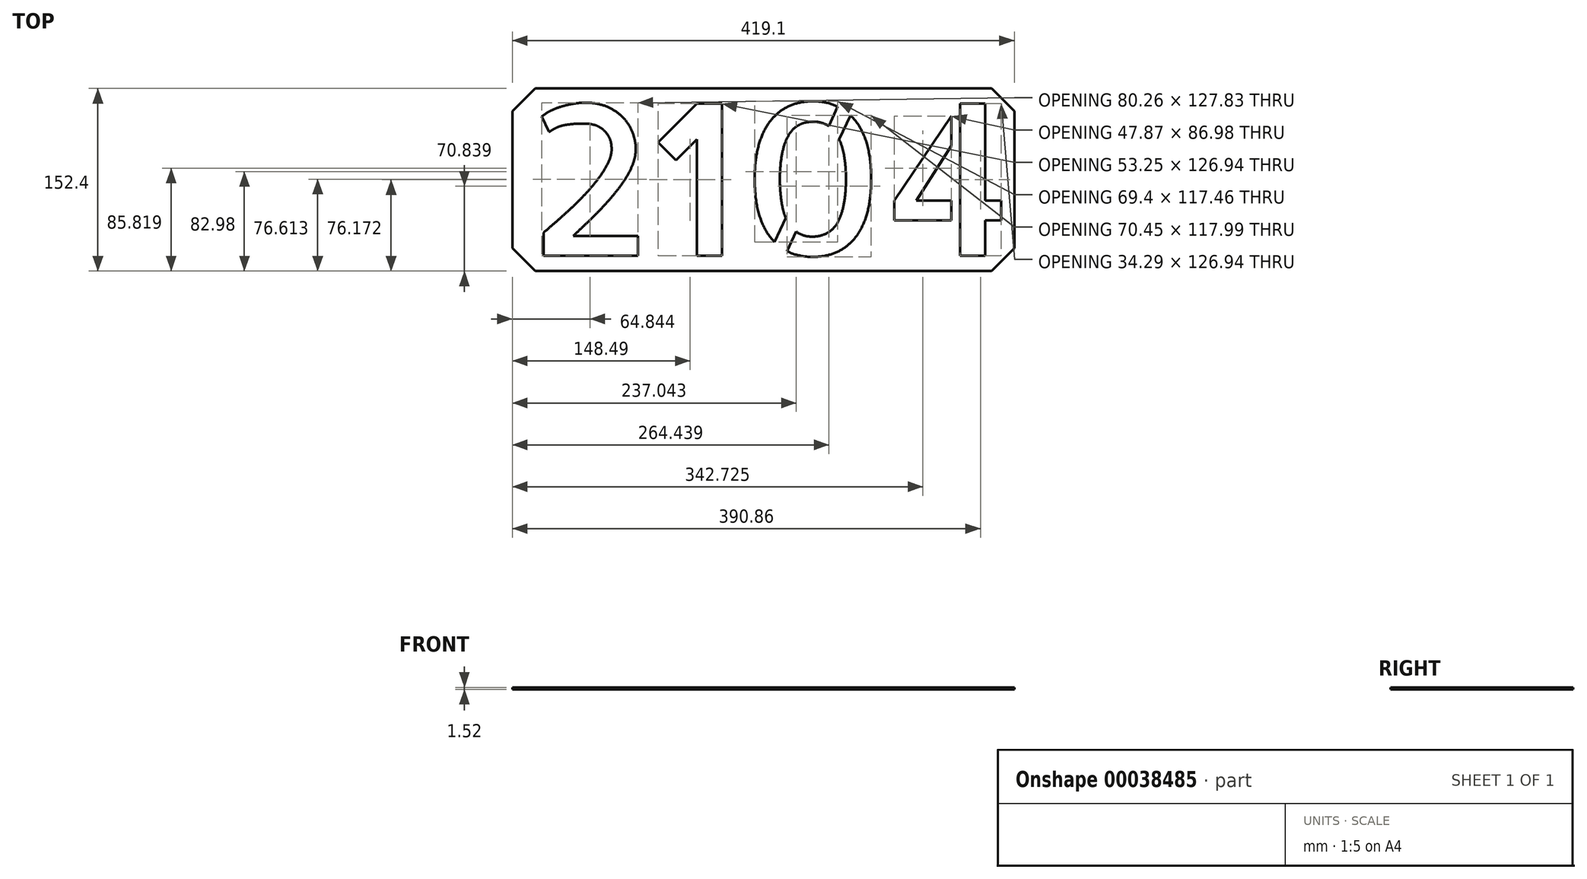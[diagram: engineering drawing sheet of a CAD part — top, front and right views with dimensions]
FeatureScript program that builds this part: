
annotation { "Feature Type Name" : "Feature", "Feature Type Description" : "" }
export const myFeature = defineFeature(function(context is Context, id is Id, definition is map)
    precondition{}
    {
        {
            var Q0;
            Q0=qCreatedBy(makeId("Top.planeOp"),FACE);
            var sketch = newSketch(context, id + "F0", { "sketchPlane" : qUnion([Q0])});
            skText(sketch, "E0", { "text": "2104", "fontName": "AllertaStencil-Regular.ttf"});
            const initialGuessF0  = {"E0": [-0.19845, -0.0635, 1, 0, 0.127]};
            skSetInitialGuess(sketch, initialGuessF0);
            skSolve(sketch);
        }
        {
            var Q0;
            Q0=qCreatedBy(makeId("Top.planeOp"),FACE);
            var sketch = newSketch(context, id + "F1", { "sketchPlane" : qUnion([Q0])});
            skLineSegment(sketch, "E1.rect.bottom", {"start": v(209.55, -76.2) * mm, "end": v(-209.55, -76.2) * mm});
            skLineSegment(sketch, "E1.rect.top", {"start": v(209.55, 76.2) * mm, "end": v(-209.55, 76.2) * mm});
            skLineSegment(sketch, "E1.rect.left", {"start": v(209.55, -76.2) * mm, "end": v(209.55, 76.2) * mm});
            skLineSegment(sketch, "E1.rect.right", {"start": v(-209.55, -76.2) * mm, "end": v(-209.55, 76.2) * mm});
            skPoint(sketch, "E1.rect.middle", {"position": v(0, 0) * mm});
            skSolve(sketch);
        }
        {
            var Q0;
            Q0 = qSketchRegion(id + "F1", true);
            extrude(context, id + "F2", {"entities" : qUnion([Q0]), "depth" : 1.52 * mm});
        }
        {
            var Q0;
            Q0 = qSketchRegion(id + "F0", true);
            extrude(context, id + "F3", {"entities" : qUnion([Q0]), "operationType" : NewBodyOperationType.REMOVE, "depth" : 25.4 * mm});
        }
        {
            var Q0;
            Q0=makeQuery(id+"F2.opExtrude","SWEPT_EDGE",EDGE,{"disambiguationData":[OSD([sQuery(id+"F1.wireOp",EDGE,"E1.rect.bottom"),sQuery(id+"F1.wireOp",EDGE,"E1.rect.left")])]});
            var Q1;
            Q1=makeQuery(id+"F2.opExtrude","SWEPT_EDGE",EDGE,{"disambiguationData":[OSD([sQuery(id+"F1.wireOp",EDGE,"E1.rect.top"),sQuery(id+"F1.wireOp",EDGE,"E1.rect.left")])]});
            var Q2;
            Q2=makeQuery(id+"F2.opExtrude","SWEPT_EDGE",EDGE,{"disambiguationData":[OSD([sQuery(id+"F1.wireOp",EDGE,"E1.rect.bottom"),sQuery(id+"F1.wireOp",EDGE,"E1.rect.right")])]});
            var Q3;
            Q3=makeQuery(id+"F2.opExtrude","SWEPT_EDGE",EDGE,{"disambiguationData":[OSD([sQuery(id+"F1.wireOp",EDGE,"E1.rect.top"),sQuery(id+"F1.wireOp",EDGE,"E1.rect.right")])]});
            chamfer(context, id + "F4", {"entities" : qUnion([Q0, Q1, Q2, Q3]), "width" : 19.05 * mm, "tangentPropagation" : true});
        }
    });
